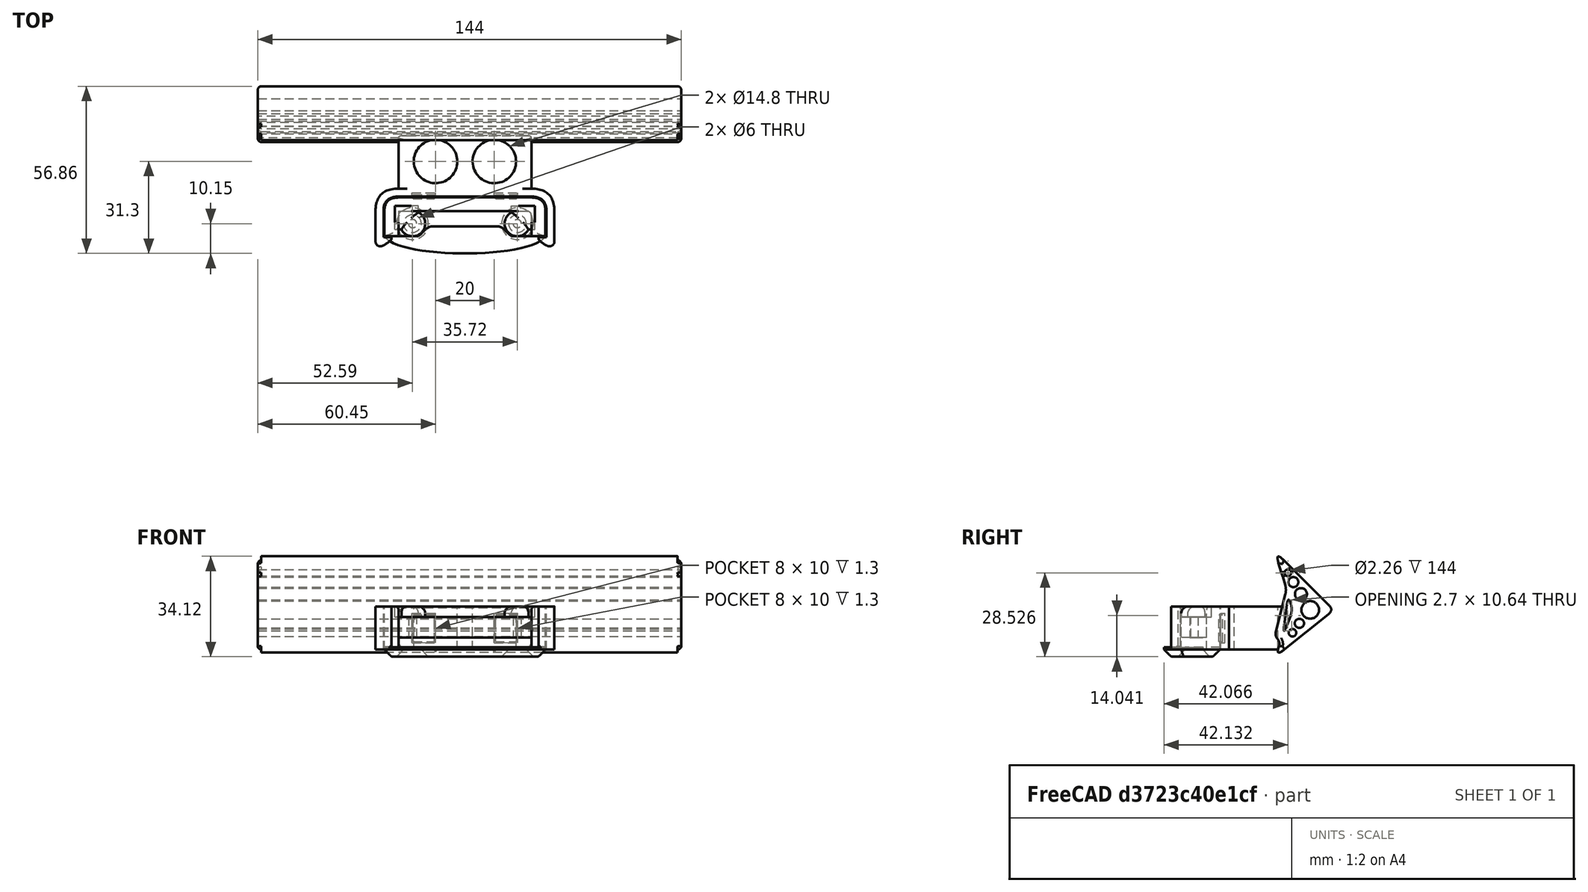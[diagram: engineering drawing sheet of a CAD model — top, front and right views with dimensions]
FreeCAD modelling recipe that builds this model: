
FCSTD DOCUMENT  (FreeCAD 0.19R0.19.2)
Label: 048
License: All rights reserved
LicenseURL: http://en.wikipedia.org/wiki/All_rights_reserved
objects: Sketcher::SketchObject×7, Part::Extrusion×7, Part::Fillet×7, Part::Box×5, Part::MultiFuse×5, Part::Cylinder×4, Part::Cut×4, Part::Chamfer×2
note: 41 computed .brp shape members not serialized (recipe doc carries the construction recipe); baked Part::Feature solids carry a one-line shape summary decoded from their .brp

FEATURE [Sketcher::SketchObject] Sketch  label="attatchmentPiece"
  FullyConstrained = true
  sketch-geometry (20):
    g0: LineSegment StartX=21.05 StartY=0 StartZ=0 EndX=21.05 EndY=-1 EndZ=0
    g1: LineSegment StartX=21.05 StartY=-1 StartZ=0 EndX=21.05 EndY=-4.3 EndZ=0
    g2: LineSegment StartX=-24.15 StartY=4.3 StartZ=0 EndX=21.05 EndY=4.3 EndZ=0
    g3: LineSegment StartX=21.05 StartY=0 StartZ=0 EndX=21.05 EndY=4.3 EndZ=0
    g4-g7: Circle x4 (B-spline internal-alignment scaffolding for g8; pole/knot coordinates omitted)
    g8: BSplineCurve PolesCount=4 KnotsCount=2 Degree=3 IsPeriodic=0
    g9: GeomPoint X=10.05 Y=-1 Z=0
    g10: GeomPoint X=14.55 Y=-4.3 Z=0
    g11: LineSegment StartX=10.05 StartY=-1 StartZ=0 EndX=-10.05 EndY=-1 EndZ=0
    g12: LineSegment StartX=14.55 StartY=-4.3 StartZ=0 EndX=21.05 EndY=-4.3 EndZ=0
    g13: LineSegment StartX=-24.15 StartY=4.3 StartZ=0 EndX=-24.15 EndY=-4.3 EndZ=0
    g14: LineSegment StartX=-13.15 StartY=-1 StartZ=0 EndX=-10.05 EndY=-1 EndZ=0
    g15: LineSegment StartX=-24.15 StartY=-4.3 StartZ=0 EndX=-19.35 EndY=-4.3 EndZ=0
    g16: LineSegment StartX=-19.35 StartY=-4.3 StartZ=0 EndX=-17.65 EndY=-4.3 EndZ=0
    g17: BSplineCurve PolesCount=4 KnotsCount=2 Degree=3 IsPeriodic=0
    g18: Circle CenterX=16.25 CenterY=0 CenterZ=0 NormalX=0 NormalY=0 NormalZ=1 AngleXU=0 Radius=1.4
    g19: Circle CenterX=-19.35 CenterY=0 CenterZ=0 NormalX=0 NormalY=0 NormalZ=1 AngleXU=0 Radius=1.4
  constraints (41):
    c: Vertical(g0)
    c: Coincident(g1,g0)
    c: Vertical(g1)
    c: Block(g0)
    c: Horizontal(g2)
    c: Vertical(g3)
    c: Coincident(g3,g2)
    c: Block(g2)
    c: Block(g3)
    c: Weight(g4) = 1
    c: Equal(g4,g5)
    c: Equal(g4,g6)
    c: Equal(g4,g7)
    c: InternalAlignment(g4-g7 -> g8) x4
    c: InternalAlignment(g9,g8)
    c: InternalAlignment(g10,g8)
    c: Block(g8)
    c: Coincident(g11,g8)
    c: Horizontal(g11)
    c: Coincident(g12,g8)
    c: Coincident(g12,g1)
    c: Horizontal(g12)
    c: Distance(g2) = 45.2
    c: Coincident(g13,g2)
    c: Vertical(g13)
    c: Horizontal(g14)
    c: Distance(g14) = 3.1
    c: Horizontal(g15)
    c: Block(g17)
    c: Coincident(g16,g15)
    c: Coincident(g16,g17)
    c: Horizontal(g16)
    c: Block(g16)
    c: Coincident(g17,g14)
    c: Block(g15)
    c: Block(g11)
    c: Block(g13)
    c: Distance(g15) = 4.8
    c: Distance(g16) = 1.7
    c: Block(g18)
    c: Block(g19)
FEATURE [Part::Extrusion] Extrude  label="attatchmentPiece001"
  Base = -> Sketch
  Dir = (0,0,1)
  DirMode = 2
  FaceMakerClass = Part::FaceMakerBullseye
  LengthFwd = 7
  LengthRev = 0
  Solid = true
  Symmetric = false
FEATURE [Sketcher::SketchObject] Sketch001  label="attatchmentPieceSurround"
  FullyConstrained = true
  sketch-geometry (18):
    g0: LineSegment StartX=25.85 StartY=-4.3 StartZ=0 EndX=21.05 EndY=-4.3 EndZ=0
    g1: LineSegment StartX=25.85 StartY=-4.3 StartZ=0 EndX=25.85 EndY=4.3 EndZ=0
    g2: LineSegment StartX=-21.05 StartY=8.9 StartZ=0 EndX=21.05 EndY=8.9 EndZ=0
    g3: Circle CenterX=21.05 CenterY=8.9 CenterZ=0 NormalX=0 NormalY=0 NormalZ=1 AngleXU=0 Radius=1
    g4: Circle CenterX=25.85 CenterY=8.9 CenterZ=0 NormalX=0 NormalY=0 NormalZ=1 AngleXU=0 Radius=1
    g5: Circle CenterX=25.85 CenterY=4.3 CenterZ=0 NormalX=0 NormalY=0 NormalZ=1 AngleXU=0 Radius=1
    g6: BSplineCurve PolesCount=3 KnotsCount=2 Degree=2 IsPeriodic=0
    g7: GeomPoint X=21.05 Y=8.9 Z=0
    g8: GeomPoint X=25.85 Y=4.3 Z=0
    g9: ArcOfCircle CenterX=19.45 CenterY=2.7 CenterZ=0 NormalX=0 NormalY=0 NormalZ=1 AngleXU=0 Radius=1.6 StartAngle=0 EndAngle=1.5708
    g10: LineSegment StartX=21.05 StartY=2.7 StartZ=0 EndX=21.05 EndY=-4.3 EndZ=0
    g11: BSplineCurve PolesCount=3 KnotsCount=2 Degree=2 IsPeriodic=0
    g12: LineSegment StartX=-28.95 StartY=-4.3 StartZ=0 EndX=-28.95 EndY=4.3 EndZ=0
    g13: LineSegment StartX=-24.15 StartY=-4.3 StartZ=0 EndX=-28.95 EndY=-4.3 EndZ=0
    g14: LineSegment StartX=-24.15 StartY=2.7 StartZ=0 EndX=-24.15 EndY=-4.3 EndZ=0
    g15: ArcOfCircle CenterX=-22.55 CenterY=2.7 CenterZ=0 NormalX=0 NormalY=0 NormalZ=1 AngleXU=0 Radius=1.6 StartAngle=1.5708 EndAngle=3.14159
    g16: LineSegment StartX=-24.15 StartY=8.9 StartZ=0 EndX=-21.05 EndY=8.9 EndZ=0
    g17: LineSegment StartX=-22.55 StartY=4.3 StartZ=0 EndX=19.45 EndY=4.3 EndZ=0
  constraints (38):
    c: Horizontal(g0)
    c: Vertical(g1)
    c: Coincident(g1,g0)
    c: Horizontal(g2)
    c: Distance(g2) = 42.1
    c: Block(g2)
    c: Coincident(g6,g2)
    c: Weight(g3) = 1
    c: Equal(g3,g4)
    c: Equal(g3,g5)
    c: Coincident(g6,g1)
    c: InternalAlignment(g3,g6)
    c: InternalAlignment(g4,g6)
    c: InternalAlignment(g5,g6)
    c: InternalAlignment(g7,g6)
    c: InternalAlignment(g8,g6)
    c: Block(g0)
    c: Block(g6)
    c: Block(g9)
    c: Coincident(g10,g9)
    c: Coincident(g10,g0)
    c: Vertical(g10)
    c: Horizontal(g13)
    c: Coincident(g12,g13)
    c: Vertical(g12)
    c: Coincident(g11,g12)
    c: Block(g12)
    c: Block(g11)
    c: Block(g15)
    c: Coincident(g14,g15)
    c: Coincident(g14,g13)
    c: Vertical(g14)
    c: Coincident(g16,g11)
    c: Coincident(g16,g2)
    c: Horizontal(g16)
    c: Coincident(g17,g15)
    c: Coincident(g17,g9)
    c: Horizontal(g17)
FEATURE [Part::Extrusion] Extrude001  label="attatchmentPieceSurround001"
  Base = -> Sketch001
  Dir = (0,0,1)
  DirMode = 2
  FaceMakerClass = Part::FaceMakerBullseye
  LengthFwd = 14.7
  LengthRev = 0
  Placement = pos=(0,0,-4.1) rot=(0,0,1;0rad)
  Solid = true
  Symmetric = false
FEATURE [Sketcher::SketchObject] Sketch002  label="attatchmentPieceEndScrewHoleCaps"
  FullyConstrained = true
  sketch-geometry (10):
    g0: ArcOfCircle CenterX=16.25 CenterY=0 CenterZ=0 NormalX=0 NormalY=0 NormalZ=1 AngleXU=0 Radius=4.3 StartAngle=2.05456 EndAngle=5.79942
    g1: LineSegment StartX=14.25 StartY=3.80657 StartZ=0 EndX=14.25 EndY=6 EndZ=0
    g2: LineSegment StartX=20.0566 StartY=-2 StartZ=0 EndX=22.25 EndY=-2 EndZ=0
    g3: LineSegment StartX=22.25 StartY=-2 StartZ=0 EndX=22.25 EndY=6 EndZ=0
    g4: LineSegment StartX=14.25 StartY=6 StartZ=0 EndX=22.25 EndY=6 EndZ=0
    g5: LineSegment StartX=-25.35 StartY=-2 StartZ=0 EndX=-25.35 EndY=6 EndZ=0
    g6: LineSegment StartX=-25.35 StartY=-2 StartZ=0 EndX=-23.1566 EndY=-2 EndZ=0
    g7: LineSegment StartX=-17.35 StartY=6 StartZ=0 EndX=-25.35 EndY=6 EndZ=0
    g8: LineSegment StartX=-17.35 StartY=3.80657 StartZ=0 EndX=-17.35 EndY=6 EndZ=0
    g9: ArcOfCircle CenterX=-19.35 CenterY=0 CenterZ=0 NormalX=0 NormalY=0 NormalZ=1 AngleXU=0 Radius=4.3 StartAngle=3.62536 EndAngle=7.37022
  constraints (25):
    c: Block(g0)
    c: Vertical(g1)
    c: Horizontal(g2)
    c: Coincident(g3,g2)
    c: Vertical(g3)
    c: Coincident(g4,g1)
    c: Horizontal(g4)
    c: Coincident(g3,g4)
    c: Block(g4)
    c: Block(g3)
    c: Coincident(g0,g1)
    c: Coincident(g0,g2)
    c: Block(g1)
    c: Block(g9)
    c: Horizontal(g6)
    c: Vertical(g8)
    c: Coincident(g7,g8)
    c: Horizontal(g7)
    c: Coincident(g5,g6)
    c: Vertical(g5)
    c: Coincident(g5,g7)
    c: Block(g7)
    c: Block(g5)
    c: Coincident(g9,g6)
    c: Coincident(g9,g8)
FEATURE [Part::Extrusion] Extrude002  label="attatchmentPieceEndScrewHoleCaps001"
  Base = -> Sketch002
  Dir = (0,0,1)
  DirMode = 2
  FaceMakerClass = Part::FaceMakerBullseye
  LengthFwd = 3.6
  LengthRev = 0
  Placement = pos=(0,0,7) rot=(0,0,1;0rad)
  Solid = true
  Symmetric = false
FEATURE [Sketcher::SketchObject] Sketch003  label="mainBumpperPieceAttatchment"
  FullyConstrained = true
  sketch-geometry (42):
    g0: Circle CenterX=28.85 CenterY=4.3 CenterZ=0 NormalX=0 NormalY=0 NormalZ=1 AngleXU=0 Radius=1
    g1: Circle CenterX=28.85 CenterY=11.9 CenterZ=0 NormalX=0 NormalY=0 NormalZ=1 AngleXU=0 Radius=1
    g2: Circle CenterX=21.05 CenterY=11.9 CenterZ=0 NormalX=0 NormalY=0 NormalZ=1 AngleXU=0 Radius=1
    g3: BSplineCurve PolesCount=3 KnotsCount=2 Degree=2 IsPeriodic=0
    g4: GeomPoint X=28.85 Y=4.3 Z=0
    g5: GeomPoint X=21.05 Y=11.9 Z=0
    g6: LineSegment StartX=-21.05 StartY=11.9 StartZ=0 EndX=21.05 EndY=11.9 EndZ=0
    g7: LineSegment StartX=28.85 StartY=4.3 StartZ=0 EndX=28.85 EndY=-4.3 EndZ=0
    g8: Circle CenterX=21.05 CenterY=9.2 CenterZ=0 NormalX=0 NormalY=0 NormalZ=1 AngleXU=0 Radius=1
    g9: Circle CenterX=26.15 CenterY=9.2 CenterZ=0 NormalX=0 NormalY=0 NormalZ=1 AngleXU=0 Radius=1
    g10: Circle CenterX=26.15 CenterY=4.3 CenterZ=0 NormalX=0 NormalY=0 NormalZ=1 AngleXU=0 Radius=1
    g11: BSplineCurve PolesCount=3 KnotsCount=2 Degree=2 IsPeriodic=0
    g12: GeomPoint X=21.05 Y=9.2 Z=0
    g13: GeomPoint X=26.15 Y=4.3 Z=0
    g14: LineSegment StartX=-21.05 StartY=9.2 StartZ=0 EndX=21.05 EndY=9.2 EndZ=0
    g15: LineSegment StartX=26.15 StartY=-4.3 StartZ=0 EndX=26.15 EndY=4.3 EndZ=0
    g16: LineSegment StartX=26.15 StartY=-4.3 StartZ=0 EndX=26.15 EndY=-4.6 EndZ=0
    g17: LineSegment StartX=23.45 StartY=-4.6 StartZ=0 EndX=26.15 EndY=-4.6 EndZ=0
    g18: LineSegment StartX=28.85 StartY=-4.3 StartZ=0 EndX=28.85 EndY=-7.9 EndZ=0
    g19: LineSegment StartX=23.45 StartY=-4.6 StartZ=0 EndX=23.45 EndY=-5.3 EndZ=0
    g20: Circle CenterX=28.85 CenterY=-7.9 CenterZ=0 NormalX=0 NormalY=0 NormalZ=1 AngleXU=0 Radius=1
    g21: Circle CenterX=26.15 CenterY=-8.2 CenterZ=0 NormalX=0 NormalY=0 NormalZ=1 AngleXU=0 Radius=1
    g22: Circle CenterX=23.45 CenterY=-5.3 CenterZ=0 NormalX=0 NormalY=0 NormalZ=1 AngleXU=0 Radius=1
    g23: BSplineCurve PolesCount=3 KnotsCount=2 Degree=2 IsPeriodic=0
    g24: GeomPoint X=28.85 Y=-7.9 Z=0
    g25: GeomPoint X=23.45 Y=-5.3 Z=0
    g26: LineSegment StartX=-21.05 StartY=9.2 StartZ=0 EndX=-24.15 EndY=9.2 EndZ=0
    g27: BSplineCurve PolesCount=3 KnotsCount=2 Degree=2 IsPeriodic=0
    g28: LineSegment StartX=-29.25 StartY=-4.3 StartZ=0 EndX=-29.25 EndY=-4.6 EndZ=0
    g29: LineSegment StartX=-29.25 StartY=-4.6 StartZ=0 EndX=-26.55 EndY=-4.6 EndZ=0
    g30: LineSegment StartX=-31.95 StartY=-4.3 StartZ=0 EndX=-31.95 EndY=-7.9 EndZ=0
    g31: LineSegment StartX=-26.55 StartY=-4.6 StartZ=0 EndX=-26.55 EndY=-5.3 EndZ=0
    g32: Circle CenterX=-31.95 CenterY=-7.9 CenterZ=0 NormalX=0 NormalY=0 NormalZ=1 AngleXU=0 Radius=1
    g33: Circle CenterX=-29.25 CenterY=-8.2 CenterZ=0 NormalX=0 NormalY=0 NormalZ=1 AngleXU=0 Radius=1
    g34: Circle CenterX=-26.55 CenterY=-5.3 CenterZ=0 NormalX=0 NormalY=0 NormalZ=1 AngleXU=0 Radius=1
    g35: BSplineCurve PolesCount=3 KnotsCount=2 Degree=2 IsPeriodic=0
    g36: GeomPoint X=-31.95 Y=-7.9 Z=0
    g37: GeomPoint X=-26.55 Y=-5.3 Z=0
    g38: LineSegment StartX=-31.95 StartY=4.3 StartZ=0 EndX=-31.95 EndY=-4.3 EndZ=0
    g39: LineSegment StartX=-29.25 StartY=-4.3 StartZ=0 EndX=-29.25 EndY=4.3 EndZ=0
    g40: BSplineCurve PolesCount=3 KnotsCount=2 Degree=2 IsPeriodic=0
    g41: LineSegment StartX=-21.05 StartY=11.9 StartZ=0 EndX=-24.15 EndY=11.9 EndZ=0
  constraints (78):
    c: Weight(g0) = 1
    c: Equal(g0,g1)
    c: Equal(g0,g2)
    c: InternalAlignment(g0,g3)
    c: InternalAlignment(g1,g3)
    c: InternalAlignment(g2,g3)
    c: InternalAlignment(g4,g3)
    c: InternalAlignment(g5,g3)
    c: Block(g3)
    c: Horizontal(g6)
    c: Vertical(g7)
    c: Block(g7)
    c: Block(g6)
    c: Weight(g8) = 1
    c: Equal(g8,g9)
    c: Equal(g8,g10)
    c: InternalAlignment(g8,g11)
    c: InternalAlignment(g9,g11)
    c: InternalAlignment(g10,g11)
    c: InternalAlignment(g12,g11)
    c: InternalAlignment(g13,g11)
    c: Horizontal(g14)
    c: Vertical(g15)
    c: Block(g11)
    c: Block(g15)
    c: Block(g14)
    c: Coincident(g16,g15)
    c: Vertical(g16)
    c: Distance(g16) = 0.3
    c: Horizontal(g17)
    c: Coincident(g17,g16)
    c: Coincident(g18,g7)
    c: Vertical(g18)
    c: Distance(g18) = 3.6
    c: Vertical(g19)
    c: Coincident(g19,g17)
    c: Coincident(g23,g18)
    c: Weight(g20) = 1
    c: Equal(g20,g21)
    c: Equal(g20,g22)
    c: Coincident(g23,g19)
    c: InternalAlignment(g20,g23)
    c: InternalAlignment(g21,g23)
    c: InternalAlignment(g22,g23)
    c: InternalAlignment(g24,g23)
    c: InternalAlignment(g25,g23)
    c: Block(g23)
    c: Horizontal(g26)
    c: Distance(g26) = 3.1
    c: Block(g27)
    c: Vertical(g38)
    c: Block(g38)
    c: Vertical(g39)
    c: Block(g40)
    c: Block(g39)
    c: Vertical(g28)
    c: Coincident(g28,g39)
    c: Coincident(g29,g28)
    c: Horizontal(g29)
    c: Vertical(g30)
    c: Coincident(g30,g38)
    c: Coincident(g31,g29)
    c: Vertical(g31)
    c: Coincident(g35,g30)
    c: Equal(g32,g33)
    c: Equal(g32,g34)
    c: Coincident(g35,g31)
    c: InternalAlignment(g32,g35)
    c: InternalAlignment(g33,g35)
    c: InternalAlignment(g34,g35)
    c: InternalAlignment(g36,g35)
    c: InternalAlignment(g37,g35)
    c: Block(g35)
    c: Coincident(g40,g26)
    c: Block(g29)
    c: Horizontal(g41)
    c: Equal(g26,g41) = 3.1
    c: Coincident(g41,g6)
FEATURE [Part::Box] Box  label="bumpperExtension"
  AttacherType = Attacher::AttachEngine3D
  Height = 14.7
  Length = 45.2
  Placement = pos=(-24.15,11.9,-4.1) rot=(0,0,1;0rad)
  Width = 18
FEATURE [Sketcher::SketchObject] Sketch004  label="bumpperMain"
  FullyConstrained = true
  Placement = pos=(0,0,0) rot=(0.57735,0.57735,0.57735;2.0944rad)
  sketch-geometry (62):
    g0: Circle CenterX=-3.12329 CenterY=2.49901 CenterZ=0 NormalX=0 NormalY=0 NormalZ=1 AngleXU=0 Radius=1
    g1: Circle CenterX=0 CenterY=0 CenterZ=0 NormalX=0 NormalY=0 NormalZ=1 AngleXU=0 Radius=1
    g2: Circle CenterX=-1.35243 CenterY=3.60648 CenterZ=0 NormalX=0 NormalY=0 NormalZ=1 AngleXU=0 Radius=1
    g3: BSplineCurve PolesCount=3 KnotsCount=2 Degree=2 IsPeriodic=0
    g4: GeomPoint X=-3.12329 Y=2.49901 Z=0
    g5: GeomPoint X=-1.35243 Y=3.60648 Z=0
    g6: Circle CenterX=-2.83953 CenterY=33.0261 CenterZ=0 NormalX=0 NormalY=0 NormalZ=1 AngleXU=0 Radius=1
    g7: Circle CenterX=0 CenterY=35.8434 CenterZ=0 NormalX=0 NormalY=0 NormalZ=1 AngleXU=0 Radius=1
    g8: Circle CenterX=-1.15771 CenterY=32.0146 CenterZ=0 NormalX=0 NormalY=0 NormalZ=1 AngleXU=0 Radius=1
    g9: BSplineCurve PolesCount=3 KnotsCount=2 Degree=2 IsPeriodic=0
    g10: GeomPoint X=-2.83953 Y=33.0261 Z=0
    g11: GeomPoint X=-1.15771 Y=32.0146 Z=0
    g12: Circle CenterX=-18.2963 CenterY=17.6904 CenterZ=0 NormalX=0 NormalY=0 NormalZ=1 AngleXU=0 Radius=1
    g13: Circle CenterX=-20 CenterY=16 CenterZ=0 NormalX=0 NormalY=0 NormalZ=1 AngleXU=0 Radius=1
    g14: Circle CenterX=-18.1259 CenterY=14.5008 CenterZ=0 NormalX=0 NormalY=0 NormalZ=1 AngleXU=0 Radius=1
    g15: BSplineCurve PolesCount=3 KnotsCount=2 Degree=2 IsPeriodic=0
    g16: GeomPoint X=-18.2963 Y=17.6904 Z=0
    g17: GeomPoint X=-18.1259 Y=14.5008 Z=0
    g18: LineSegment StartX=-18.2963 StartY=17.6904 StartZ=0 EndX=-2.83953 EndY=33.0261 EndZ=0
    g19: LineSegment StartX=-18.1259 StartY=14.5008 StartZ=0 EndX=-3.12329 EndY=2.49901 EndZ=0
    g20: Circle CenterX=-11.9527 CenterY=16 CenterZ=0 NormalX=0 NormalY=0 NormalZ=1 AngleXU=0 Radius=2.99582
    g21: Circle CenterX=-8.803 CenterY=21.3731 CenterZ=0 NormalX=0 NormalY=0 NormalZ=1 AngleXU=0 Radius=2.03939
    g22: Circle CenterX=-6.23123 CenterY=25.4475 CenterZ=0 NormalX=0 NormalY=0 NormalZ=1 AngleXU=0 Radius=1.69309
    g23: Circle CenterX=-4.38186 CenterY=28.6261 CenterZ=0 NormalX=0 NormalY=0 NormalZ=1 AngleXU=0 Radius=1.13029
    g24: Circle CenterX=-8.28033 CenterY=11.4296 CenterZ=0 NormalX=0 NormalY=0 NormalZ=1 AngleXU=0 Radius=1.57213
    g25: Circle CenterX=-5.93972 CenterY=8.22213 CenterZ=0 NormalX=0 NormalY=0 NormalZ=1 AngleXU=0 Radius=1.28743
    g26: Circle CenterX=-3.47023 CenterY=24.3665 CenterZ=0 NormalX=0 NormalY=0 NormalZ=1 AngleXU=0 Radius=1
    g27: Circle CenterX=-3.90437 CenterY=22.9307 CenterZ=0 NormalX=0 NormalY=0 NormalZ=1 AngleXU=0 Radius=1
    g28: Circle CenterX=-3.53772 CenterY=21.4762 CenterZ=0 NormalX=0 NormalY=0 NormalZ=1 AngleXU=0 Radius=1
    g29: BSplineCurve PolesCount=3 KnotsCount=2 Degree=2 IsPeriodic=0
    g30: GeomPoint X=-3.47023 Y=24.3665 Z=0
    g31: GeomPoint X=-3.53772 Y=21.4762 Z=0
    g32: LineSegment StartX=-1.15771 StartY=32.0146 StartZ=0 EndX=-3.47023 EndY=24.3665 EndZ=0
    g33: Circle CenterX=-5.41867 CenterY=17.9226 CenterZ=0 NormalX=0 NormalY=0 NormalZ=1 AngleXU=0 Radius=1
    g34: Circle CenterX=-6 CenterY=16 CenterZ=0 NormalX=0 NormalY=0 NormalZ=1 AngleXU=0 Radius=1
    g35: Circle CenterX=-5.22753 CenterY=13.9401 CenterZ=0 NormalX=0 NormalY=0 NormalZ=1 AngleXU=0 Radius=1
    g36: BSplineCurve PolesCount=3 KnotsCount=2 Degree=2 IsPeriodic=0
    g37: GeomPoint X=-5.41867 Y=17.9226 Z=0
    g38: GeomPoint X=-5.22753 Y=13.9401 Z=0
    g39: Circle CenterX=-3.98946 CenterY=10.6386 CenterZ=0 NormalX=0 NormalY=0 NormalZ=1 AngleXU=0 Radius=1
    g40: Circle CenterX=-2.58497 CenterY=6.89324 CenterZ=0 NormalX=0 NormalY=0 NormalZ=1 AngleXU=0 Radius=1
    g41: Circle CenterX=-3.11001 CenterY=10.8586 CenterZ=0 NormalX=0 NormalY=0 NormalZ=1 AngleXU=0 Radius=1
    g42: BSplineCurve PolesCount=3 KnotsCount=2 Degree=2 IsPeriodic=0
    g43: GeomPoint X=-3.98946 Y=10.6386 Z=0
    g44: GeomPoint X=-3.11001 Y=10.8586 Z=0
    g45: Circle CenterX=-1.35243 CenterY=3.60648 CenterZ=0 NormalX=0 NormalY=0 NormalZ=1 AngleXU=0 Radius=1
    g46: Circle CenterX=-1.76142 CenterY=4.69712 CenterZ=0 NormalX=0 NormalY=0 NormalZ=1 AngleXU=0 Radius=1
    g47: Circle CenterX=-1.05937 CenterY=5.79125 CenterZ=0 NormalX=0 NormalY=0 NormalZ=1 AngleXU=0 Radius=1
    g48: BSplineCurve PolesCount=3 KnotsCount=2 Degree=2 IsPeriodic=0
    g49: GeomPoint X=-1.35243 Y=3.60648 Z=0
    g50: GeomPoint X=-1.05937 Y=5.79125 Z=0
    g51: Circle CenterX=-0.519336 CenterY=6.6329 CenterZ=0 NormalX=0 NormalY=0 NormalZ=1 AngleXU=0 Radius=1
    g52: Circle CenterX=0 CenterY=7.44228 CenterZ=0 NormalX=0 NormalY=0 NormalZ=1 AngleXU=0 Radius=1
    g53: Circle CenterX=-0.244436 CenterY=8.41194 CenterZ=0 NormalX=0 NormalY=0 NormalZ=1 AngleXU=0 Radius=1
    g54: BSplineCurve PolesCount=3 KnotsCount=2 Degree=2 IsPeriodic=0
    g55: GeomPoint X=-0.519336 Y=6.6329 Z=0
    g56: GeomPoint X=-0.244436 Y=8.41194 Z=0
    g57: LineSegment StartX=-3.53772 StartY=21.4762 StartZ=0 EndX=-0.244436 EndY=8.41194 EndZ=0
    g58: LineSegment StartX=-5.22753 StartY=13.9401 StartZ=0 EndX=-3.98946 EndY=10.6386 EndZ=0
    g59: LineSegment StartX=-1.05937 StartY=5.79125 StartZ=0 EndX=-0.519336 EndY=6.6329 EndZ=0
    g60: BSplineCurve PolesCount=3 KnotsCount=2 Degree=2 IsPeriodic=0
    g61: LineSegment StartX=-4.0304 StartY=17.8099 StartZ=0 EndX=-3.11001 EndY=10.8586 EndZ=0
  constraints (96):
    c: Weight(g0) = 1
    c: Equal(g0,g1)
    c: Equal(g0,g2)
    c: InternalAlignment(g0,g3)
    c: InternalAlignment(g1,g3)
    c: InternalAlignment(g2,g3)
    c: InternalAlignment(g4,g3)
    c: InternalAlignment(g5,g3)
    c: Block(g3)
    c: Weight(g6) = 1
    c: Equal(g6,g7)
    c: Equal(g6,g8)
    c: InternalAlignment(g6,g9)
    c: InternalAlignment(g7,g9)
    c: InternalAlignment(g8,g9)
    c: InternalAlignment(g10,g9)
    c: InternalAlignment(g11,g9)
    c: Block(g9)
    c: Weight(g12) = 1
    c: Equal(g12,g13)
    c: Equal(g12,g14)
    c: InternalAlignment(g12,g15)
    c: InternalAlignment(g13,g15)
    c: InternalAlignment(g14,g15)
    c: InternalAlignment(g16,g15)
    c: InternalAlignment(g17,g15)
    c: Block(g15)
    c: Coincident(g18,g15)
    c: Coincident(g18,g9)
    c: Coincident(g19,g15)
    c: Coincident(g19,g3)
    c: Block(g25)
    c: Block(g24)
    c: Block(g20)
    c: Block(g21)
    c: Block(g22)
    c: Block(g23)
    c: Weight(g26) = 1
    c: Equal(g26,g27)
    c: Equal(g26,g28)
    c: InternalAlignment(g26,g29)
    c: InternalAlignment(g27,g29)
    c: InternalAlignment(g28,g29)
    c: InternalAlignment(g30,g29)
    c: InternalAlignment(g31,g29)
    c: Block(g29)
    c: Coincident(g32,g9)
    c: Coincident(g32,g29)
    c: Weight(g33) = 1
    c: Equal(g33,g34)
    c: Equal(g33,g35)
    c: InternalAlignment(g33,g36)
    c: InternalAlignment(g34,g36)
    c: InternalAlignment(g35,g36)
    c: InternalAlignment(g37,g36)
    c: InternalAlignment(g38,g36)
    c: Block(g36)
    c: Weight(g39) = 1
    c: Equal(g39,g40)
    c: Equal(g39,g41)
    c: InternalAlignment(g39,g42)
    c: InternalAlignment(g40,g42)
    c: InternalAlignment(g41,g42)
    c: InternalAlignment(g43,g42)
    c: InternalAlignment(g44,g42)
    c: Block(g42)
    c: Coincident(g48,g3)
    c: Weight(g45) = 1
    c: Equal(g45,g46)
    c: Equal(g45,g47)
    c: InternalAlignment(g45,g48)
    c: InternalAlignment(g46,g48)
    c: InternalAlignment(g47,g48)
    c: InternalAlignment(g49,g48)
    c: InternalAlignment(g50,g48)
    c: Block(g48)
    c: Weight(g51) = 1
    c: Equal(g51,g52)
    c: Equal(g51,g53)
    c: InternalAlignment(g51,g54)
    c: InternalAlignment(g52,g54)
    c: InternalAlignment(g53,g54)
    c: InternalAlignment(g55,g54)
    c: InternalAlignment(g56,g54)
    c: Block(g54)
    c: Coincident(g57,g29)
    c: Coincident(g57,g54)
    c: Block(g57)
    c: Coincident(g58,g36)
    c: Coincident(g58,g42)
    c: Coincident(g59,g48)
    c: Coincident(g59,g54)
    c: Block(g60)
    c: Coincident(g60,g36)
    c: Coincident(g61,g60)
    c: Coincident(g61,g42)
FEATURE [Part::Extrusion] Extrude004  label="bumpperMain001"
  Base = -> Sketch004
  Dir = (1,0,0)
  DirMode = 2
  FaceMakerClass = Part::FaceMakerBullseye
  LengthFwd = 144
  LengthRev = 0
  Placement = pos=(72,27.6,-6.6) rot=(0,0,1;3.14159rad)
  Solid = true
  Symmetric = false
FEATURE [Sketcher::SketchObject] Sketch005  label="attatchmentPieceBottom"
  FullyConstrained = true
  sketch-geometry (20):
    g0: LineSegment StartX=25.85 StartY=-4.3 StartZ=0 EndX=25.85 EndY=4.3 EndZ=0
    g1: LineSegment StartX=-21.05 StartY=8.9 StartZ=0 EndX=21.05 EndY=8.9 EndZ=0
    g2: Circle CenterX=21.05 CenterY=8.9 CenterZ=0 NormalX=0 NormalY=0 NormalZ=1 AngleXU=0 Radius=1
    g3: Circle CenterX=25.85 CenterY=8.9 CenterZ=0 NormalX=0 NormalY=0 NormalZ=1 AngleXU=0 Radius=1
    g4: Circle CenterX=25.85 CenterY=4.3 CenterZ=0 NormalX=0 NormalY=0 NormalZ=1 AngleXU=0 Radius=1
    g5: BSplineCurve PolesCount=3 KnotsCount=2 Degree=2 IsPeriodic=0
    g6: GeomPoint X=21.05 Y=8.9 Z=0
    g7: GeomPoint X=25.85 Y=4.3 Z=0
    g8: BSplineCurve PolesCount=3 KnotsCount=2 Degree=2 IsPeriodic=0
    g9: LineSegment StartX=-28.95 StartY=-4.3 StartZ=0 EndX=-28.95 EndY=4.3 EndZ=0
    g10: LineSegment StartX=-24.15 StartY=8.9 StartZ=0 EndX=-21.05 EndY=8.9 EndZ=0
    g11: Circle CenterX=-19.41 CenterY=0 CenterZ=0 NormalX=0 NormalY=0 NormalZ=1 AngleXU=0 Radius=3
    g12: Circle CenterX=16.3103 CenterY=0 CenterZ=0 NormalX=0 NormalY=0 NormalZ=1 AngleXU=0 Radius=3
    g13-g16: Circle x4 (B-spline internal-alignment scaffolding for g17; pole/knot coordinates omitted)
    g17: BSplineCurve PolesCount=4 KnotsCount=2 Degree=3 IsPeriodic=0
    g18: GeomPoint X=-28.95 Y=-4.3 Z=0
    g19: GeomPoint X=25.85 Y=-4.3 Z=0
  constraints (36):
    c: Vertical(g0)
    c: Horizontal(g1)
    c: Distance(g1) = 42.1
    c: Block(g1)
    c: Coincident(g5,g1)
    c: Weight(g2) = 1
    c: Equal(g2,g3)
    c: Equal(g2,g4)
    c: Coincident(g5,g0)
    c: InternalAlignment(g2,g5)
    c: InternalAlignment(g3,g5)
    c: InternalAlignment(g4,g5)
    c: InternalAlignment(g6,g5)
    c: InternalAlignment(g7,g5)
    c: Block(g5)
    c: Vertical(g9)
    c: Coincident(g8,g9)
    c: Block(g9)
    c: Block(g8)
    c: Coincident(g10,g8)
    c: Coincident(g10,g1)
    c: Horizontal(g10)
    c: PointOnObject(g12,g-1)
    c: PointOnObject(g11,g-1)
    c: Block(g11)
    c: Block(g12)
    c: Coincident(g17,g9)
    c: Weight(g13) = 1
    c: Equal(g13,g14)
    c: Equal(g13,g15)
    c: Equal(g13,g16)
    c: Coincident(g17,g0)
    c: InternalAlignment(g13-g16 -> g17) x4
    c: InternalAlignment(g18,g17)
    c: InternalAlignment(g19,g17)
    c: Block(g17)
FEATURE [Part::Extrusion] Extrude005  label="removeFromMainBumpperPieceAttatchment"
  Base = -> Sketch005
  Dir = (0,0,1)
  DirMode = 2
  FaceMakerClass = Part::FaceMakerBullseye
  LengthFwd = 3.2
  LengthRev = 0
  Placement = pos=(0,0,-6.2) rot=(0,0,1;0rad)
  Solid = true
  Symmetric = false
FEATURE [Part::Extrusion] Extrude006  label="mainBumpperPieceAttatchment001"
  Base = -> Sketch003
  Dir = (0,0,1)
  DirMode = 2
  FaceMakerClass = Part::FaceMakerBullseye
  LengthFwd = 14.7
  LengthRev = 0
  Placement = pos=(0,0,-4.1) rot=(0,0,1;0rad)
  Solid = true
  Symmetric = false
FEATURE [Part::Cylinder] Cylinder  label="removeFromBumpperExtension"
  Angle = 360
  AttacherType = Attacher::AttachEngine3D
  Height = 20
  Placement = pos=(8.45,21.15,-8) rot=(0,0,1;0rad)
  Radius = 7.4
FEATURE [Part::Cylinder] Cylinder001  label="removeFromBumpperExtension001"
  Angle = 360
  AttacherType = Attacher::AttachEngine3D
  Height = 20
  Placement = pos=(-11.55,21.15,-8) rot=(0,0,1;0rad)
  Radius = 7.4
FEATURE [Part::MultiFuse] Fusion  label="removeFromBumpperExtension002"
  Shapes = -> [Cylinder,Cylinder001]
FEATURE [Part::Cylinder] Cylinder002  label="removeFromBumpperExtension004"
  Angle = 360
  AttacherType = Attacher::AttachEngine3D
  Height = 20
  Placement = pos=(8.45,21.15,-8) rot=(0,0,1;0rad)
  Radius = 7.4
FEATURE [Part::Cylinder] Cylinder003  label="removeFromBumpperExtension005"
  Angle = 360
  AttacherType = Attacher::AttachEngine3D
  Height = 20
  Placement = pos=(-11.55,21.15,-8) rot=(0,0,1;0rad)
  Radius = 7.4
FEATURE [Part::MultiFuse] Fusion001  label="removeFromBumpperMain"
  Shapes = -> [Cylinder002,Cylinder003]
FEATURE [Part::Cut] Cut  label="bumpperExtension001"
  Base = -> Box
  Tool = -> Fusion
FEATURE [Part::Cut] Cut001  label="bumpperMain002"
  Base = -> Extrude004
  Tool = -> Fusion001
FEATURE [Part::Fillet] Fillet  label="bumpperExtension002"
  Base = -> Cut
  Edges = 4 edges r=3: [Edge2,Edge4,Edge9,Edge14]
FEATURE [Part::Fillet] Fillet001
  Base = -> Cut001
  Edges = 11 edges r=1.2: [Edge4,Edge7,Edge10,Edge30,Edge31,Edge32,Edge33,Edge34,Edge35,Edge36,Edge37]
FEATURE [Part::Fillet] Fillet002  label="bumpperMain003"
  Base = -> Fillet001
  Edges = 11 edges r=1.2: [Edge4,Edge9,Edge13,Edge14,Edge15,Edge16,Edge17,Edge18,Edge19,Edge20,Edge21]
FEATURE [Part::Box] Box001  label="bumpperExtensionBumpHole"
  AttacherType = Attacher::AttachEngine3D
  Height = 10
  Length = 8
  Placement = pos=(8.45,9.2,-1.8) rot=(0,0,1;0rad)
  Width = 1.3
FEATURE [Part::Box] Box002  label="bumpperExtensionBumpHole001"
  AttacherType = Attacher::AttachEngine3D
  Height = 10
  Length = 8
  Placement = pos=(-19.55,9.2,-1.8) rot=(0,0,1;0rad)
  Width = 1.3
FEATURE [Part::Box] Box003  label="attatchmentPieceSurroundBump"
  AttacherType = Attacher::AttachEngine3D
  Height = 9.2
  Length = 7.2
  Placement = pos=(8.85,8.9,-1.4) rot=(0,0,1;0rad)
  Width = 1.3
FEATURE [Part::Box] Box004  label="attatchmentPieceSurroundBump001"
  AttacherType = Attacher::AttachEngine3D
  Height = 9.2
  Length = 7.2
  Placement = pos=(-19.15,8.9,-1.4) rot=(0,0,1;0rad)
  Width = 1.3
FEATURE [Part::MultiFuse] Fusion002  label="attatchmentPieceSurroundBump002"
  Placement = pos=(0,-0.4,0) rot=(0,0,1;0rad)
  Shapes = -> [Box004,Box003]
FEATURE [Part::MultiFuse] Fusion003  label="bumpperExtensionBumpHole002"
  Shapes = -> [Box002,Box001]
FEATURE [Part::Cut] Cut002  label="mainBumpperPieceAttatchment002"
  Base = -> Extrude006
  Tool = -> Fusion003
FEATURE [Part::Fillet] Fillet003  label="attatchmentPieceEndScrewHoleCaps002"
  Base = -> Extrude002
  Edges = 6 edges r=2.4: [Edge4,Edge7,Edge15,Edge25,Edge28,Edge30]
FEATURE [Part::Fillet] Fillet004  label="attatchmentPieceSurround002"
  Base = -> Extrude001
  Edges = 3 edges r=1.2: [Edge19,Edge25,Edge31]
FEATURE [Part::Fillet] Fillet006  label="mainBumpperPieceAttatchment003"
  Base = -> Cut002
  Edges = 2 edges r=1.6: [Edge2,Edge55]
FEATURE [Sketcher::SketchObject] Sketch006  label="attatchmentPieceBottom002"
  FullyConstrained = true
  sketch-geometry (20):
    g0: LineSegment StartX=25.85 StartY=-4.3 StartZ=0 EndX=25.85 EndY=4.3 EndZ=0
    g1: LineSegment StartX=-21.05 StartY=8.9 StartZ=0 EndX=21.05 EndY=8.9 EndZ=0
    g2: Circle CenterX=21.05 CenterY=8.9 CenterZ=0 NormalX=0 NormalY=0 NormalZ=1 AngleXU=0 Radius=1
    g3: Circle CenterX=25.85 CenterY=8.9 CenterZ=0 NormalX=0 NormalY=0 NormalZ=1 AngleXU=0 Radius=1
    g4: Circle CenterX=25.85 CenterY=4.3 CenterZ=0 NormalX=0 NormalY=0 NormalZ=1 AngleXU=0 Radius=1
    g5: BSplineCurve PolesCount=3 KnotsCount=2 Degree=2 IsPeriodic=0
    g6: GeomPoint X=21.05 Y=8.9 Z=0
    g7: GeomPoint X=25.85 Y=4.3 Z=0
    g8: BSplineCurve PolesCount=3 KnotsCount=2 Degree=2 IsPeriodic=0
    g9: LineSegment StartX=-28.95 StartY=-4.3 StartZ=0 EndX=-28.95 EndY=4.3 EndZ=0
    g10: LineSegment StartX=-24.15 StartY=8.9 StartZ=0 EndX=-21.05 EndY=8.9 EndZ=0
    g11: Circle CenterX=-19.41 CenterY=0 CenterZ=0 NormalX=0 NormalY=0 NormalZ=1 AngleXU=0 Radius=3
    g12: Circle CenterX=16.3103 CenterY=0 CenterZ=0 NormalX=0 NormalY=0 NormalZ=1 AngleXU=0 Radius=3
    g13-g16: Circle x4 (B-spline internal-alignment scaffolding for g17; pole/knot coordinates omitted)
    g17: BSplineCurve PolesCount=4 KnotsCount=2 Degree=3 IsPeriodic=0
    g18: GeomPoint X=-28.95 Y=-4.3 Z=0
    g19: GeomPoint X=25.85 Y=-4.3 Z=0
  constraints (36):
    c: Vertical(g0)
    c: Horizontal(g1)
    c: Distance(g1) = 42.1
    c: Block(g1)
    c: Coincident(g5,g1)
    c: Weight(g2) = 1
    c: Equal(g2,g3)
    c: Equal(g2,g4)
    c: Coincident(g5,g0)
    c: InternalAlignment(g2,g5)
    c: InternalAlignment(g3,g5)
    c: InternalAlignment(g4,g5)
    c: InternalAlignment(g6,g5)
    c: InternalAlignment(g7,g5)
    c: Block(g5)
    c: Vertical(g9)
    c: Coincident(g8,g9)
    c: Block(g9)
    c: Block(g8)
    c: Coincident(g10,g8)
    c: Coincident(g10,g1)
    c: Horizontal(g10)
    c: PointOnObject(g12,g-1)
    c: PointOnObject(g11,g-1)
    c: Block(g11)
    c: Block(g12)
    c: Coincident(g17,g9)
    c: Weight(g13) = 1
    c: Equal(g13,g14)
    c: Equal(g13,g15)
    c: Equal(g13,g16)
    c: Coincident(g17,g0)
    c: InternalAlignment(g13-g16 -> g17) x4
    c: InternalAlignment(g18,g17)
    c: InternalAlignment(g19,g17)
    c: Block(g17)
FEATURE [Part::Extrusion] Extrude007  label="attatchmentPieceBottom003"
  Base = -> Sketch006
  Dir = (0,0,1)
  DirMode = 2
  FaceMakerClass = Part::FaceMakerBullseye
  LengthFwd = 3.2
  LengthRev = 0
  Placement = pos=(0,0,-6.5) rot=(0,0,1;0rad)
  Solid = true
  Symmetric = false
FEATURE [Part::Cut] Cut003  label="mainBumpperPieceAttatchment004"
  Base = -> Fillet006
  Tool = -> Extrude005
FEATURE [Part::Chamfer] Chamfer
  Base = -> Extrude007
  Edges = 2 edges r=2.4: [Edge23,Edge26]
FEATURE [Part::Chamfer] Chamfer001  label="attatchmentPieceBottom004"
  Base = -> Chamfer
  Edges = 7 edges r=2.4: [Edge14,Edge15,Edge16,Edge17,Edge18,Edge19,Edge20]
FEATURE [Part::Fillet] Fillet007  label="attatchmentPieceBottom005"
  Base = -> Chamfer001
  Edges = 7 edges r=1.2: [Edge1,Edge2,Edge3,Edge4,Edge5,Edge6,Edge7]
FEATURE [Part::MultiFuse] Fusion006
  Shapes = -> [Fillet002,Fillet,Cut003]
